FCSTD DOCUMENT  (FreeCAD 0.16R6698 (Git))
Label: pnp mount plate
License: All rights reserved
LicenseURL: http://en.wikipedia.org/wiki/All_rights_reserved
objects: Sketcher::SketchObject×4
note: 4 computed .brp shape members not serialized (recipe doc carries the construction recipe); baked Part::Feature solids carry a one-line shape summary decoded from their .brp

FEATURE [Sketcher::SketchObject] Sketch
  sketch-geometry (117):
    g0: LineSegment StartX=490 StartY=-10.8666 StartZ=0 EndX=-10 EndY=-10.8666 EndZ=0
    g1: LineSegment StartX=-10 StartY=-10.8666 StartZ=0 EndX=-10 EndY=289.133 EndZ=0
    g2: LineSegment StartX=-10 StartY=289.133 StartZ=0 EndX=490 EndY=289.133 EndZ=0
    g3: LineSegment StartX=490 StartY=289.133 StartZ=0 EndX=490 EndY=-10.8666 EndZ=0
    g4: Circle CenterX=0 CenterY=280 CenterZ=0 NormalX=0 NormalY=0 NormalZ=1 Radius=2.5
    g5: Circle CenterX=0 CenterY=0 CenterZ=0 NormalX=0 NormalY=0 NormalZ=1 Radius=2.5
    g6: Circle CenterX=480 CenterY=0 CenterZ=0 NormalX=0 NormalY=0 NormalZ=1 Radius=2.5
    g7: Circle CenterX=480 CenterY=280 CenterZ=0 NormalX=0 NormalY=0 NormalZ=1 Radius=2.5
    g8: Circle CenterX=240 CenterY=280 CenterZ=0 NormalX=0 NormalY=0 NormalZ=1 Radius=2.5
    g9: Circle CenterX=240 CenterY=0 CenterZ=0 NormalX=0 NormalY=0 NormalZ=1 Radius=2.5
    g10: Circle CenterX=480 CenterY=140 CenterZ=0 NormalX=0 NormalY=0 NormalZ=1 Radius=2.5
    g11: Circle CenterX=0 CenterY=140 CenterZ=0 NormalX=0 NormalY=0 NormalZ=1 Radius=2.5
    g12: Circle CenterX=240 CenterY=140 CenterZ=0 NormalX=0 NormalY=0 NormalZ=1 Radius=2.5
    g13: Circle CenterX=20 CenterY=240 CenterZ=0 NormalX=0 NormalY=0 NormalZ=1 Radius=1.5
    g14: Circle CenterX=20 CenterY=200 CenterZ=0 NormalX=0 NormalY=0 NormalZ=1 Radius=1.5
    g15: Circle CenterX=20 CenterY=160 CenterZ=0 NormalX=0 NormalY=0 NormalZ=1 Radius=1.5
    g16: Circle CenterX=20 CenterY=120 CenterZ=0 NormalX=0 NormalY=0 NormalZ=1 Radius=1.5
    g17: Circle CenterX=20 CenterY=80 CenterZ=0 NormalX=0 NormalY=0 NormalZ=1 Radius=1.5
    g18: Circle CenterX=20 CenterY=40 CenterZ=0 NormalX=0 NormalY=0 NormalZ=1 Radius=1.5
    g19: Circle CenterX=60 CenterY=80 CenterZ=0 NormalX=0 NormalY=0 NormalZ=1 Radius=1.5
    g20: Circle CenterX=100 CenterY=80 CenterZ=0 NormalX=0 NormalY=0 NormalZ=1 Radius=1.5
    g21: Circle CenterX=140 CenterY=80 CenterZ=0 NormalX=0 NormalY=0 NormalZ=1 Radius=1.5
    g22: Circle CenterX=180 CenterY=80 CenterZ=0 NormalX=0 NormalY=0 NormalZ=1 Radius=1.5
    g23: Circle CenterX=60 CenterY=40 CenterZ=0 NormalX=0 NormalY=0 NormalZ=1 Radius=1.5
    g24: Circle CenterX=100 CenterY=40 CenterZ=0 NormalX=0 NormalY=0 NormalZ=1 Radius=1.5
    g25: Circle CenterX=140 CenterY=40 CenterZ=0 NormalX=0 NormalY=0 NormalZ=1 Radius=1.5
    g26: Circle CenterX=180 CenterY=40 CenterZ=0 NormalX=0 NormalY=0 NormalZ=1 Radius=1.5
    g27: Circle CenterX=220 CenterY=80 CenterZ=0 NormalX=0 NormalY=0 NormalZ=1 Radius=1.5
    g28: Circle CenterX=260 CenterY=80 CenterZ=0 NormalX=0 NormalY=0 NormalZ=1 Radius=1.5
    g29: Circle CenterX=220 CenterY=40 CenterZ=0 NormalX=0 NormalY=0 NormalZ=1 Radius=1.5
    g30: Circle CenterX=260 CenterY=40 CenterZ=0 NormalX=0 NormalY=0 NormalZ=1 Radius=1.5
    g31: Circle CenterX=300 CenterY=80 CenterZ=0 NormalX=0 NormalY=0 NormalZ=1 Radius=1.5
    g32: Circle CenterX=300 CenterY=40 CenterZ=0 NormalX=0 NormalY=0 NormalZ=1 Radius=1.5
    g33: Circle CenterX=340 CenterY=80 CenterZ=0 NormalX=0 NormalY=0 NormalZ=1 Radius=1.5
    g34: Circle CenterX=340 CenterY=40 CenterZ=0 NormalX=0 NormalY=0 NormalZ=1 Radius=1.5
    g35: Circle CenterX=380 CenterY=80 CenterZ=0 NormalX=0 NormalY=0 NormalZ=1 Radius=1.5
    g36: Circle CenterX=380 CenterY=40 CenterZ=0 NormalX=0 NormalY=0 NormalZ=1 Radius=1.5
    g37: Circle CenterX=420 CenterY=80 CenterZ=0 NormalX=0 NormalY=0 NormalZ=1 Radius=1.5
    g38: Circle CenterX=420 CenterY=40 CenterZ=0 NormalX=0 NormalY=0 NormalZ=1 Radius=1.5
    g39: Circle CenterX=460 CenterY=80 CenterZ=0 NormalX=0 NormalY=0 NormalZ=1 Radius=1.5
    g40: Circle CenterX=460 CenterY=40 CenterZ=0 NormalX=0 NormalY=0 NormalZ=1 Radius=1.5
    g41: Circle CenterX=60 CenterY=120 CenterZ=0 NormalX=0 NormalY=0 NormalZ=1 Radius=1.5
    g42: Circle CenterX=100 CenterY=120 CenterZ=0 NormalX=0 NormalY=0 NormalZ=1 Radius=1.5
    g43: Circle CenterX=140 CenterY=120 CenterZ=0 NormalX=0 NormalY=0 NormalZ=1 Radius=1.5
    g44: Circle CenterX=180 CenterY=120 CenterZ=0 NormalX=0 NormalY=0 NormalZ=1 Radius=1.5
    g45: Circle CenterX=220 CenterY=120 CenterZ=0 NormalX=0 NormalY=0 NormalZ=1 Radius=1.5
    g46: Circle CenterX=260 CenterY=120 CenterZ=0 NormalX=0 NormalY=0 NormalZ=1 Radius=1.5
    g47: Circle CenterX=300 CenterY=120 CenterZ=0 NormalX=0 NormalY=0 NormalZ=1 Radius=1.5
    g48: Circle CenterX=340 CenterY=120 CenterZ=0 NormalX=0 NormalY=0 NormalZ=1 Radius=1.5
    g49: Circle CenterX=460 CenterY=120 CenterZ=0 NormalX=0 NormalY=0 NormalZ=1 Radius=1.5
    g50: Circle CenterX=460 CenterY=160 CenterZ=0 NormalX=0 NormalY=0 NormalZ=1 Radius=1.5
    g51: Circle CenterX=460 CenterY=200 CenterZ=0 NormalX=0 NormalY=0 NormalZ=1 Radius=1.5
    g52: Circle CenterX=460 CenterY=240 CenterZ=0 NormalX=0 NormalY=0 NormalZ=1 Radius=1.5
    g53: Circle CenterX=460 CenterY=280 CenterZ=0 NormalX=0 NormalY=0 NormalZ=1 Radius=1.5
    g54: Circle CenterX=420 CenterY=280 CenterZ=0 NormalX=0 NormalY=0 NormalZ=1 Radius=1.5
    g55: Circle CenterX=420 CenterY=240 CenterZ=0 NormalX=0 NormalY=0 NormalZ=1 Radius=1.5
    g56: Circle CenterX=420 CenterY=200 CenterZ=0 NormalX=0 NormalY=0 NormalZ=1 Radius=1.5
    g57: Circle CenterX=420 CenterY=160 CenterZ=0 NormalX=0 NormalY=0 NormalZ=1 Radius=1.5
    g58: Circle CenterX=420 CenterY=120 CenterZ=0 NormalX=0 NormalY=0 NormalZ=1 Radius=1.5
    g59: Circle CenterX=380 CenterY=120 CenterZ=0 NormalX=0 NormalY=0 NormalZ=1 Radius=1.5
    g60: Circle CenterX=380 CenterY=160 CenterZ=0 NormalX=0 NormalY=0 NormalZ=1 Radius=1.5
    g61: Circle CenterX=380 CenterY=200 CenterZ=0 NormalX=0 NormalY=0 NormalZ=1 Radius=1.5
    g62: Circle CenterX=380 CenterY=240 CenterZ=0 NormalX=0 NormalY=0 NormalZ=1 Radius=1.5
    g63: Circle CenterX=380 CenterY=280 CenterZ=0 NormalX=0 NormalY=0 NormalZ=1 Radius=1.5
    g64: Circle CenterX=340 CenterY=280 CenterZ=0 NormalX=0 NormalY=0 NormalZ=1 Radius=1.5
    g65: Circle CenterX=340 CenterY=240 CenterZ=0 NormalX=0 NormalY=0 NormalZ=1 Radius=1.5
    g66: Circle CenterX=340 CenterY=200 CenterZ=0 NormalX=0 NormalY=0 NormalZ=1 Radius=1.5
    g67: Circle CenterX=340 CenterY=160 CenterZ=0 NormalX=0 NormalY=0 NormalZ=1 Radius=1.5
    g68: Circle CenterX=300 CenterY=160 CenterZ=0 NormalX=0 NormalY=0 NormalZ=1 Radius=1.5
    g69: Circle CenterX=300 CenterY=200 CenterZ=0 NormalX=0 NormalY=0 NormalZ=1 Radius=1.5
    g70: Circle CenterX=300 CenterY=240 CenterZ=0 NormalX=0 NormalY=0 NormalZ=1 Radius=1.5
    g71: Circle CenterX=300 CenterY=280 CenterZ=0 NormalX=0 NormalY=0 NormalZ=1 Radius=1.5
    g72: Circle CenterX=260 CenterY=280 CenterZ=0 NormalX=0 NormalY=0 NormalZ=1 Radius=1.5
    g73: Circle CenterX=260 CenterY=240 CenterZ=0 NormalX=0 NormalY=0 NormalZ=1 Radius=1.5
    g74: Circle CenterX=260 CenterY=200 CenterZ=0 NormalX=0 NormalY=0 NormalZ=1 Radius=1.5
    g75: Circle CenterX=260 CenterY=160 CenterZ=0 NormalX=0 NormalY=0 NormalZ=1 Radius=1.5
    g76: Circle CenterX=220 CenterY=160 CenterZ=0 NormalX=0 NormalY=0 NormalZ=1 Radius=1.5
    g77: Circle CenterX=180 CenterY=160 CenterZ=0 NormalX=0 NormalY=0 NormalZ=1 Radius=1.5
    g78: Circle CenterX=140 CenterY=160 CenterZ=0 NormalX=0 NormalY=0 NormalZ=1 Radius=1.5
    g79: Circle CenterX=100 CenterY=160 CenterZ=0 NormalX=0 NormalY=0 NormalZ=1 Radius=1.5
    g80: Circle CenterX=60 CenterY=160 CenterZ=0 NormalX=0 NormalY=0 NormalZ=1 Radius=1.5
    g81: Circle CenterX=60 CenterY=200 CenterZ=0 NormalX=0 NormalY=0 NormalZ=1 Radius=1.5
    g82: Circle CenterX=100 CenterY=200 CenterZ=0 NormalX=0 NormalY=0 NormalZ=1 Radius=1.5
    g83: Circle CenterX=140 CenterY=200 CenterZ=0 NormalX=0 NormalY=0 NormalZ=1 Radius=1.5
    g84: Circle CenterX=180 CenterY=200 CenterZ=0 NormalX=0 NormalY=0 NormalZ=1 Radius=1.5
    g85: Circle CenterX=220 CenterY=200 CenterZ=0 NormalX=0 NormalY=0 NormalZ=1 Radius=1.5
    g86: Circle CenterX=220 CenterY=240 CenterZ=0 NormalX=0 NormalY=0 NormalZ=1 Radius=1.5
    g87: Circle CenterX=180 CenterY=240 CenterZ=0 NormalX=0 NormalY=0 NormalZ=1 Radius=1.5
    g88: Circle CenterX=140 CenterY=240 CenterZ=0 NormalX=0 NormalY=0 NormalZ=1 Radius=1.5
    g89: Circle CenterX=100 CenterY=240 CenterZ=0 NormalX=0 NormalY=0 NormalZ=1 Radius=1.5
    g90: Circle CenterX=60 CenterY=240 CenterZ=0 NormalX=0 NormalY=0 NormalZ=1 Radius=1.5
    g91: Circle CenterX=20 CenterY=280.333 CenterZ=0 NormalX=0 NormalY=0 NormalZ=1 Radius=1.5
    g92: Circle CenterX=60 CenterY=280 CenterZ=0 NormalX=0 NormalY=0 NormalZ=1 Radius=1.5
    g93: Circle CenterX=100 CenterY=280 CenterZ=0 NormalX=0 NormalY=0 NormalZ=1 Radius=1.5
    g94: Circle CenterX=140 CenterY=280 CenterZ=0 NormalX=0 NormalY=0 NormalZ=1 Radius=1.5
    g95: Circle CenterX=180 CenterY=280 CenterZ=0 NormalX=0 NormalY=0 NormalZ=1 Radius=1.5
    g96: Circle CenterX=220 CenterY=280 CenterZ=0 NormalX=0 NormalY=0 NormalZ=1 Radius=1.5
    g97: Circle CenterX=60 CenterY=0 CenterZ=0 NormalX=0 NormalY=0 NormalZ=1 Radius=1.5
    g98: Circle CenterX=20 CenterY=0 CenterZ=0 NormalX=0 NormalY=0 NormalZ=1 Radius=1.5
    g99: Circle CenterX=100 CenterY=0 CenterZ=0 NormalX=0 NormalY=0 NormalZ=1 Radius=1.5
    g100: Circle CenterX=140 CenterY=0 CenterZ=0 NormalX=0 NormalY=0 NormalZ=1 Radius=1.5
    g101: Circle CenterX=180 CenterY=0 CenterZ=0 NormalX=0 NormalY=0 NormalZ=1 Radius=1.5
    g102: Circle CenterX=220 CenterY=0 CenterZ=0 NormalX=0 NormalY=0 NormalZ=1 Radius=1.5
    g103: Circle CenterX=260 CenterY=0 CenterZ=0 NormalX=0 NormalY=0 NormalZ=1 Radius=1.5
    g104: Circle CenterX=300 CenterY=0 CenterZ=0 NormalX=0 NormalY=0 NormalZ=1 Radius=1.5
    g105: Circle CenterX=340 CenterY=0 CenterZ=0 NormalX=0 NormalY=0 NormalZ=1 Radius=1.5
    g106: Circle CenterX=380 CenterY=0 CenterZ=0 NormalX=0 NormalY=0 NormalZ=1 Radius=1.5
    g107: Circle CenterX=420 CenterY=0 CenterZ=0 NormalX=0 NormalY=0 NormalZ=1 Radius=1.5
    g108: Circle CenterX=460 CenterY=0 CenterZ=0 NormalX=0 NormalY=0 NormalZ=1 Radius=1.5
    g109: ArcOfCircle CenterX=100.436 CenterY=140.435 CenterZ=0 NormalX=0 NormalY=0 NormalZ=1 Radius=2.6 StartAngle=2.3562 EndAngle=5.49779
    g110: ArcOfCircle CenterX=220 CenterY=260 CenterZ=0 NormalX=0 NormalY=0 NormalZ=1 Radius=2.6 StartAngle=5.49779 EndAngle=8.63939
    g111: LineSegment StartX=102.274 StartY=138.596 StartZ=0 EndX=221.838 EndY=258.162 EndZ=0
    g112: LineSegment StartX=98.5975 StartY=142.273 StartZ=0 EndX=218.162 EndY=261.838 EndZ=0
    g113: ArcOfCircle CenterX=179.987 CenterY=60.0432 CenterZ=0 NormalX=0 NormalY=0 NormalZ=1 Radius=2.6 StartAngle=2.35599 EndAngle=5.49758
    g114: ArcOfCircle CenterX=320 CenterY=200 CenterZ=0 NormalX=0 NormalY=0 NormalZ=1 Radius=2.6 StartAngle=5.49758 EndAngle=8.63918
    g115: LineSegment StartX=181.825 StartY=58.2044 StartZ=0 EndX=321.838 EndY=198.161 EndZ=0
    g116: LineSegment StartX=178.148 StartY=61.8821 StartZ=0 EndX=318.162 EndY=201.839 EndZ=0
  constraints (142):
    c: Coincident(g0,g1)
    c: Coincident(g1,g2)
    c: Coincident(g2,g3)
    c: Coincident(g3,g0)
    c: Horizontal(g0)
    c: Horizontal(g2)
    c: Vertical(g1)
    c: Vertical(g3)
    c: DistanceY(g1,g1) = 300
    c: DistanceX(g2,g2) = 500
    c: Coincident(g5,g-1)
    c: PointOnObject(g6,g-1)
    c: PointOnObject(g9,g-1)
    c: PointOnObject(g11,g-2)
    c: Equal(g4,g11)
    c: Equal(g11,g5)
    c: Equal(g5,g8)
    c: Equal(g8,g12)
    c: Equal(g12,g9)
    c: Equal(g9,g7)
    c: Equal(g7,g10)
    c: Equal(g10,g6)
    c: Radius(g4) = 2.5
    c: PointOnObject(g97,g-1)
    c: PointOnObject(g98,g-1)
    c: PointOnObject(g99,g-1)
    c: PointOnObject(g100,g-1)
    c: PointOnObject(g101,g-1)
    c: PointOnObject(g102,g-1)
    c: PointOnObject(g103,g-1)
    c: PointOnObject(g104,g-1)
    c: PointOnObject(g105,g-1)
    c: PointOnObject(g107,g-1)
    c: PointOnObject(g108,g-1)
    c: Equal(g91,g13)
    c: Equal(g13,g14)
    c: Equal(g14,g81)
    c: Equal(g81,g92)
    c: Equal(g92,g90)
    c: Equal(g90,g89)
    c: Equal(g89,g82)
    c: Equal(g82,g83)
    c: Equal(g83,g88)
    c: Equal(g88,g94)
    c: Equal(g94,g93)
    c: Equal(g93,g95)
    c: Equal(g95,g96)
    c: Equal(g96,g86)
    c: Equal(g86,g87)
    c: Equal(g87,g84)
    c: Equal(g84,g85)
    c: Equal(g85,g74)
    c: Equal(g74,g73)
    c: Equal(g73,g72)
    c: Equal(g72,g71)
    c: Equal(g71,g70)
    c: Equal(g70,g69)
    c: Equal(g69,g64)
    c: Equal(g64,g63)
    c: Equal(g63,g54)
    c: Equal(g54,g53)
    c: Equal(g53,g52)
    c: Equal(g52,g55)
    c: Equal(g55,g62)
    c: Equal(g62,g65)
    c: Equal(g65,g66)
    c: Equal(g66,g61)
    c: Equal(g61,g56)
    c: Equal(g56,g51)
    c: Equal(g51,g50)
    c: Equal(g50,g57)
    c: Equal(g57,g60)
    c: Equal(g60,g67)
    c: Equal(g67,g68)
    c: Equal(g68,g75)
    c: Equal(g75,g76)
    c: Equal(g76,g77)
    c: Equal(g77,g78)
    c: Equal(g78,g79)
    c: Equal(g79,g80)
    c: Equal(g80,g15)
    c: Equal(g15,g49)
    c: Equal(g49,g58)
    c: Equal(g58,g59)
    c: Equal(g59,g48)
    c: Equal(g48,g47)
    c: Equal(g47,g46)
    c: Equal(g46,g45)
    c: Equal(g45,g44)
    c: Equal(g44,g43)
    c: Equal(g43,g42)
    c: Equal(g42,g41)
    c: Equal(g41,g16)
    c: Equal(g16,g17)
    c: Equal(g17,g19)
    c: Equal(g19,g20)
    c: Equal(g20,g21)
    c: Equal(g21,g22)
    c: Equal(g22,g27)
    c: Equal(g27,g28)
    c: Equal(g28,g31)
    c: Equal(g31,g33)
    c: Equal(g33,g35)
    c: Equal(g35,g37)
    c: Equal(g37,g39)
    c: Equal(g39,g40)
    c: Equal(g40,g38)
    c: Equal(g38,g36)
    c: Equal(g36,g34)
    c: Equal(g34,g32)
    c: Equal(g32,g30)
    c: Equal(g30,g29)
    c: Equal(g29,g26)
    c: Equal(g26,g25)
    c: Equal(g25,g24)
    c: Equal(g24,g23)
    c: Equal(g23,g18)
    c: Equal(g18,g98)
    c: Equal(g98,g97)
    c: Equal(g97,g99)
    c: Equal(g99,g100)
    c: Equal(g100,g101)
    c: Equal(g101,g102)
    c: Equal(g102,g103)
    c: Equal(g103,g104)
    c: Equal(g104,g105)
    c: Equal(g105,g106)
    c: Equal(g106,g107)
    c: Equal(g107,g108)
    c: Radius(g91) = 1.5
    c: Tangent(g109,g112) = 1.5708
    c: Tangent(g109,g111) = -1.5708
    c: Tangent(g111,g110) = -1.5708
    c: Tangent(g112,g110) = 1.5708
    c: Equal(g109,g110)
    c: Radius(g110) = 2.6
    c: Tangent(g113,g116) = 1.5708
    c: Tangent(g113,g115) = -1.5708
    c: Tangent(g115,g114) = -1.5708
    c: Tangent(g116,g114) = 1.5708
    c: Equal(g113,g114)
    c: Equal(g113,g110)
FEATURE [Sketcher::SketchObject] Sketch001
  sketch-geometry (4):
    g0: LineSegment StartX=33.5176 StartY=192.336 StartZ=0 EndX=233.518 EndY=192.336 EndZ=0
    g1: LineSegment StartX=233.518 StartY=192.336 StartZ=0 EndX=233.518 EndY=92.3363 EndZ=0
    g2: LineSegment StartX=233.518 StartY=92.3363 StartZ=0 EndX=33.5176 EndY=92.3363 EndZ=0
    g3: LineSegment StartX=33.5176 StartY=92.3363 StartZ=0 EndX=33.5176 EndY=192.336 EndZ=0
  constraints (10):
    c: Coincident(g0,g1)
    c: Coincident(g1,g2)
    c: Coincident(g2,g3)
    c: Coincident(g3,g0)
    c: Horizontal(g0)
    c: Horizontal(g2)
    c: Vertical(g1)
    c: Vertical(g3)
    c: DistanceX(g0,g0) = 200
    c: DistanceY(g3,g3) = 100
FEATURE [Sketcher::SketchObject] Sketch002
  sketch-geometry (2):
    g0: LineSegment StartX=0 StartY=140 StartZ=0 EndX=480 EndY=140 EndZ=0
    g1: LineSegment StartX=240 StartY=280 StartZ=0 EndX=240 EndY=0 EndZ=0
  constraints (2):
    c: Horizontal(g0)
    c: Vertical(g1)
FEATURE [Sketcher::SketchObject] Sketch003
  sketch-geometry (4):
    g0: LineSegment StartX=253.172 StartY=244.282 StartZ=0 EndX=473.172 EndY=244.282 EndZ=0
    g1: LineSegment StartX=473.172 StartY=244.282 StartZ=0 EndX=473.172 EndY=74.2824 EndZ=0
    g2: LineSegment StartX=473.172 StartY=74.2824 StartZ=0 EndX=253.172 EndY=74.2824 EndZ=0
    g3: LineSegment StartX=253.172 StartY=74.2824 StartZ=0 EndX=253.172 EndY=244.282 EndZ=0
  constraints (10):
    c: Coincident(g0,g1)
    c: Coincident(g1,g2)
    c: Coincident(g2,g3)
    c: Coincident(g3,g0)
    c: Horizontal(g0)
    c: Horizontal(g2)
    c: Vertical(g1)
    c: Vertical(g3)
    c: DistanceX(g0,g0) = 220
    c: DistanceY(g3,g3) = 170
